# Revit family: Jelly Tavolino-LivingDivani
name_source: partatom
category: Furniture
revit_build: Autodesk Revit 2013 (Build: 20130531_2115(x64)
units: mm (PartAtom-declared; Revit-internal decimal feet)

## types (9) — shared parameters
Manufacturer = LivingDivani
Mat. Struttura = Steel, Polished
Mat. Tavolo = Porcelain, Linen
Model = Jelly Tavolino
URL = http://www.livingdivani.it
raggio superiore = 21 cm

## per-type parameters (varying)
| type | 4 gambe | 5 gambe | Altezza | Codice prodotto | Raggio tavolino | altezza gamba | altezza interna | lunghezza gamba | raggio sotto tavolino |
| H32 diametro 60cm | Yes | No | 32 cm | JELV060C | 30 cm | 29 cm | 30 cm | 20 cm | 24 cm |
| H32 diametro 85cm | Yes | No | 32 cm | JELV085C | 43 cm | 29 cm | 30 cm | 33 cm | 37 cm |
| H32 diametro 100cm | Yes | No | 32 cm | JELV100C | 50 cm | 29 cm | 30 cm | 40 cm | 44 cm |
| H50 diametro 60cm | Yes | No | 50 cm | JELV0605C | 30 cm | 47 cm | 48 cm | 20 cm | 24 cm |
| H50 diametro 85cm | Yes | No | 50 cm | JELV0855C | 43 cm | 47 cm | 48 cm | 33 cm | 37 cm |
| H50 diametro 100cm | Yes | No | 50 cm | JELV1005C | 50 cm | 47 cm | 48 cm | 40 cm | 44 cm |
| H72 diametro 85cm | No | Yes | 72 cm | JELV0857C | 43 cm | 69 cm | 70 cm | 33 cm | 37 cm |
| H72 diametro 100cm | No | Yes | 72 cm | JELV1007C | 50 cm | 69 cm | 70 cm | 40 cm | 44 cm |
| H72 diametro 80cm | Yes | No | 72 cm | JELV8087X | 40 cm | 69 cm | 70 cm | 30 cm | 34 cm |

## geometry (parser evidence)
native form markers: Blend x10
no freeform markers — native parametric forms only
